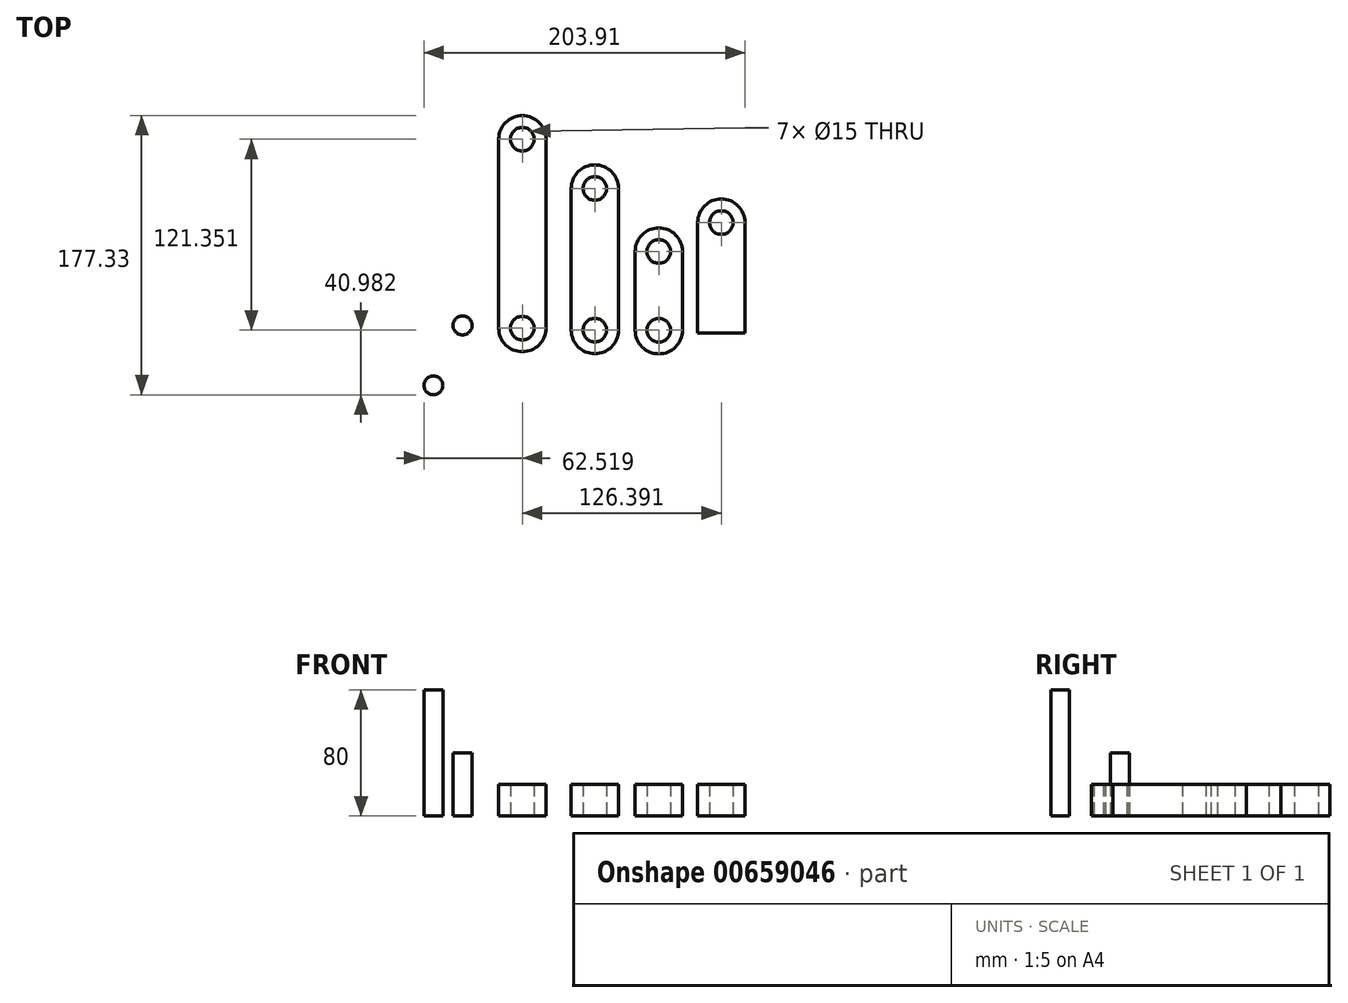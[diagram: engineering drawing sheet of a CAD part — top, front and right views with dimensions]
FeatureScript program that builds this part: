
annotation { "Feature Type Name" : "Feature", "Feature Type Description" : "" }
export const myFeature = defineFeature(function(context is Context, id is Id, definition is map)
    precondition{}
    {
        {
            assignVariable(context, id + "F0", {"name" : "thickness", "anyValue" : 20});
        }
        {
            var Q0;
            Q0=qCreatedBy(makeId("Top.planeOp"),FACE);
            var sketch = newSketch(context, id + "F1", { "sketchPlane" : qUnion([Q0])});
            skLineSegment(sketch, "E0.bottom", {"start": v(0, 0) * mm, "end": v(30, 0) * mm});
            skLineSegment(sketch, "E0.left", {"start": v(0, 0) * mm, "end": v(0, 70) * mm});
            skLineSegment(sketch, "E0.right", {"start": v(30, 0) * mm, "end": v(30, 70) * mm});
            skArc(sketch, "E1", {"start": v(30, 70) * mm, "mid": v(15, 85) * mm, "end": v(0, 70) * mm});
            skCircle(sketch, "E2", {"center": v(15, 70) * mm, "radius": 7.5 * mm});
            skSolve(sketch);
        }
        {
            var Q0;
            Q0=makeQuery(id+"F1.imprint","IMPRINT",FACE,{"disambiguationData":[TD([[makeQuery(id+"F1.imprint","IMPRINT",EDGE,{"derivedFrom":sQuery(id+"F1.wireOp",EDGE,"E0.bottom")}),1.0]])]});
            extrude(context, id + "F2", {"entities" : qUnion([Q0]), "depth" : (getVariable(context, 'thickness')) * mm, "offsetDistance" : 25 * mm});
        }
        {
            var Q0;
            Q0=qCreatedBy(makeId("Top.planeOp"),FACE);
            var sketch = newSketch(context, id + "F3", { "sketchPlane" : qUnion([Q0])});
            skLineSegment(sketch, "E3.left", {"start": v(-39.72, 1.6) * mm, "end": v(-39.72, 51.6) * mm});
            skLineSegment(sketch, "E3.right", {"start": v(-9.72, 1.6) * mm, "end": v(-9.72, 51.6) * mm});
            skArc(sketch, "E4", {"start": v(-9.72, 51.6) * mm, "mid": v(-24.72, 66.6) * mm, "end": v(-39.72, 51.6) * mm});
            skCircle(sketch, "E5", {"center": v(-24.72, 51.6) * mm, "radius": 7.5 * mm});
            skArc(sketch, "E6", {"start": v(-39.72, 1.6) * mm, "mid": v(-24.72, -13.4) * mm, "end": v(-9.72, 1.6) * mm});
            skCircle(sketch, "E7", {"center": v(-24.72, 1.6) * mm, "radius": 7.5 * mm});
            skSolve(sketch);
        }
        {
            var Q0;
            Q0=makeQuery(id+"F3.imprint","IMPRINT",FACE,{"disambiguationData":[TD([[makeQuery(id+"F3.imprint","IMPRINT",EDGE,{"derivedFrom":sQuery(id+"F3.wireOp",EDGE,"E3.left")}),-1.0]])]});
            extrude(context, id + "F4", {"entities" : qUnion([Q0]), "depth" : (getVariable(context, 'thickness')) * mm, "offsetDistance" : 25 * mm});
        }
        {
            var Q0;
            Q0=qCreatedBy(makeId("Top.planeOp"),FACE);
            var sketch = newSketch(context, id + "F5", { "sketchPlane" : qUnion([Q0])});
            skLineSegment(sketch, "E8.left", {"start": v(-80.33, 1.67) * mm, "end": v(-80.33, 91.67) * mm});
            skLineSegment(sketch, "E8.right", {"start": v(-50.33, 1.67) * mm, "end": v(-50.33, 91.67) * mm});
            skArc(sketch, "E9", {"start": v(-50.33, 91.67) * mm, "mid": v(-65.33, 106.67) * mm, "end": v(-80.33, 91.67) * mm});
            skCircle(sketch, "E10", {"center": v(-65.33, 91.67) * mm, "radius": 7.5 * mm});
            skArc(sketch, "E11", {"start": v(-80.33, 1.67) * mm, "mid": v(-65.33, -13.33) * mm, "end": v(-50.33, 1.67) * mm});
            skCircle(sketch, "E12", {"center": v(-65.33, 1.67) * mm, "radius": 7.5 * mm});
            skSolve(sketch);
        }
        {
            var Q0;
            Q0=makeQuery(id+"F5.imprint","IMPRINT",FACE,{"disambiguationData":[TD([[makeQuery(id+"F5.imprint","IMPRINT",EDGE,{"derivedFrom":sQuery(id+"F5.wireOp",EDGE,"E8.left")}),-1.0]])]});
            extrude(context, id + "F6", {"entities" : qUnion([Q0]), "depth" : (getVariable(context, 'thickness')) * mm, "offsetDistance" : 25 * mm});
        }
        {
            var Q0;
            Q0=qCreatedBy(makeId("Top.planeOp"),FACE);
            var sketch = newSketch(context, id + "F7", { "sketchPlane" : qUnion([Q0])});
            skLineSegment(sketch, "E13.left", {"start": v(-126.4, 2.95) * mm, "end": v(-126.4, 122.95) * mm});
            skLineSegment(sketch, "E13.right", {"start": v(-96.4, 2.95) * mm, "end": v(-96.4, 122.95) * mm});
            skArc(sketch, "E14", {"start": v(-96.4, 122.95) * mm, "mid": v(-111.4, 137.95) * mm, "end": v(-126.4, 122.95) * mm});
            skCircle(sketch, "E15", {"center": v(-111.4, 122.95) * mm, "radius": 7.5 * mm});
            skArc(sketch, "E16", {"start": v(-126.4, 2.95) * mm, "mid": v(-111.4, -12.05) * mm, "end": v(-96.4, 2.95) * mm});
            skCircle(sketch, "E17", {"center": v(-111.4, 2.95) * mm, "radius": 7.5 * mm});
            skSolve(sketch);
        }
        {
            var Q0;
            Q0=makeQuery(id+"F7.imprint","IMPRINT",FACE,{"disambiguationData":[TD([[makeQuery(id+"F7.imprint","IMPRINT",EDGE,{"derivedFrom":sQuery(id+"F7.wireOp",EDGE,"E13.left")}),-1.0]])]});
            extrude(context, id + "F8", {"entities" : qUnion([Q0]), "depth" : (getVariable(context, 'thickness')) * mm, "offsetDistance" : 25 * mm});
        }
        {
            var Q0;
            Q0=qCreatedBy(makeId("Top.planeOp"),FACE);
            var sketch = newSketch(context, id + "F9", { "sketchPlane" : qUnion([Q0])});
            skCircle(sketch, "E18", {"center": v(-149.37, 4.64) * mm, "radius": 6 * mm});
            skSolve(sketch);
        }
        {
            var Q0;
            Q0=makeQuery(id+"F9.imprint","IMPRINT",FACE,{"disambiguationData":[TD([[makeQuery(id+"F9.imprint","IMPRINT",EDGE,{"derivedFrom":sQuery(id+"F9.wireOp",EDGE,"E18")}),1.0]])]});
            extrude(context, id + "F10", {"entities" : qUnion([Q0]), "depth" : (getVariable(context, 'thickness') * 2) * mm, "offsetDistance" : 25 * mm});
        }
        {
            var Q0;
            Q0=qCreatedBy(makeId("Top.planeOp"),FACE);
            var sketch = newSketch(context, id + "F11", { "sketchPlane" : qUnion([Q0])});
            skCircle(sketch, "E19", {"center": v(-167.9, -33.38) * mm, "radius": 6 * mm});
            skSolve(sketch);
        }
        {
            var Q0;
            Q0=makeQuery(id+"F11.imprint","IMPRINT",FACE,{"disambiguationData":[TD([[makeQuery(id+"F11.imprint","IMPRINT",EDGE,{"derivedFrom":sQuery(id+"F11.wireOp",EDGE,"E19")}),1.0]])]});
            extrude(context, id + "F12", {"entities" : qUnion([Q0]), "depth" : (getVariable(context, 'thickness') * 4) * mm, "offsetDistance" : 25 * mm});
        }
    });
